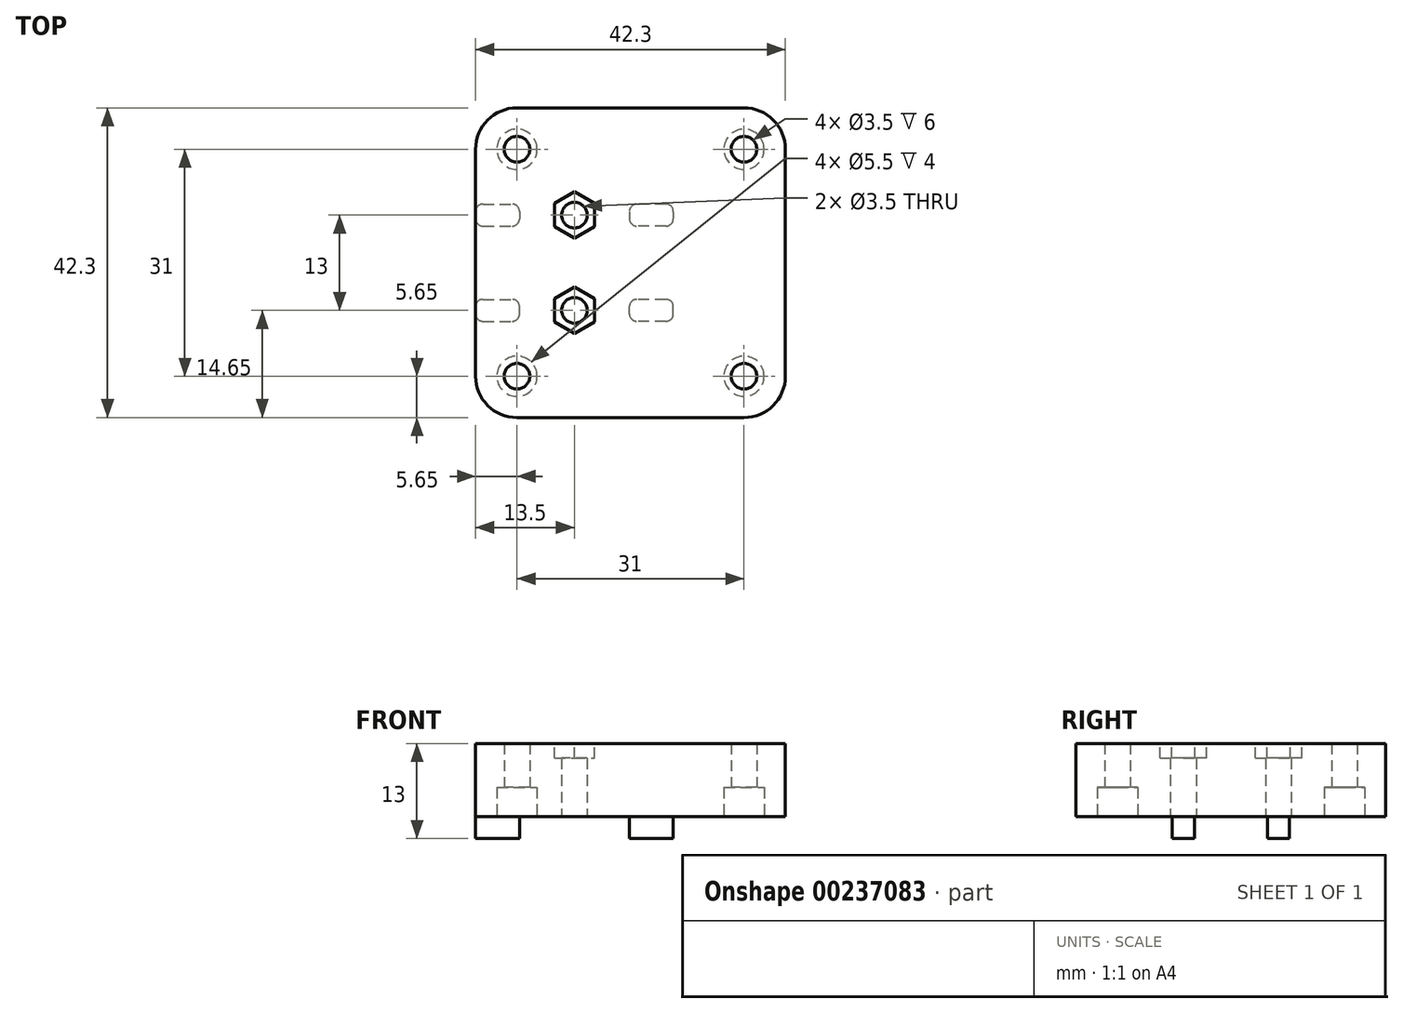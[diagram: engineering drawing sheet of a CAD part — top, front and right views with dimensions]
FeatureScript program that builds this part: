
annotation { "Feature Type Name" : "Feature", "Feature Type Description" : "" }
export const myFeature = defineFeature(function(context is Context, id is Id, definition is map)
    precondition{}
    {
        {
            var Q0;
            Q0=qCreatedBy(makeId("Top.planeOp"),FACE);
            var sketch = newSketch(context, id + "F0", { "sketchPlane" : qUnion([Q0])});
            skLineSegment(sketch, "E0.bottom", {"start": v(15.5, -15.5) * mm, "end": v(-15.5, -15.5) * mm, "construction": true});
            skLineSegment(sketch, "E0.top", {"start": v(15.5, 15.5) * mm, "end": v(-15.5, 15.5) * mm, "construction": true});
            skLineSegment(sketch, "E0.left", {"start": v(15.5, -15.5) * mm, "end": v(15.5, 15.5) * mm, "construction": true});
            skLineSegment(sketch, "E0.right", {"start": v(-15.5, -15.5) * mm, "end": v(-15.5, 15.5) * mm, "construction": true});
            skPoint(sketch, "E0.middle", {"position": v(0, 0) * mm});
            skCircle(sketch, "E1", {"center": v(-15.5, 15.5) * mm, "radius": 1.75 * mm});
            skCircle(sketch, "E2", {"center": v(15.5, 15.5) * mm, "radius": 1.75 * mm});
            skCircle(sketch, "E3", {"center": v(15.5, -15.5) * mm, "radius": 1.75 * mm});
            skCircle(sketch, "E4", {"center": v(-15.5, -15.5) * mm, "radius": 1.75 * mm});
            skLineSegment(sketch, "E5.bottom", {"start": v(15.5, -21.15) * mm, "end": v(-15.5, -21.15) * mm});
            skLineSegment(sketch, "E5.top", {"start": v(15.5, 21.15) * mm, "end": v(-15.5, 21.15) * mm});
            skLineSegment(sketch, "E5.left", {"start": v(21.15, -15.5) * mm, "end": v(21.15, 15.5) * mm});
            skLineSegment(sketch, "E5.right", {"start": v(-21.15, -15.5) * mm, "end": v(-21.15, 15.5) * mm});
            skPoint(sketch, "E6.visualSharp", {"position": v(-21.15, 21.15) * mm});
            skArc(sketch, "E6.filletArc", {"start": v(-15.5, 21.15) * mm, "mid": v(-19.5, 19.5) * mm, "end": v(-21.15, 15.5) * mm});
            skPoint(sketch, "E7.visualSharp", {"position": v(-21.15, -21.15) * mm});
            skArc(sketch, "E7.filletArc", {"start": v(-21.15, -15.5) * mm, "mid": v(-19.5, -19.5) * mm, "end": v(-15.5, -21.15) * mm});
            skPoint(sketch, "E8.visualSharp", {"position": v(21.15, -21.15) * mm});
            skArc(sketch, "E8.filletArc", {"start": v(15.5, -21.15) * mm, "mid": v(19.5, -19.5) * mm, "end": v(21.15, -15.5) * mm});
            skPoint(sketch, "E9.visualSharp", {"position": v(21.15, 21.15) * mm});
            skArc(sketch, "E9.filletArc", {"start": v(21.15, 15.5) * mm, "mid": v(19.5, 19.5) * mm, "end": v(15.5, 21.15) * mm});
            skSolve(sketch);
        }
        {
            var Q0;
            Q0=makeQuery(id+"F0.imprint","IMPRINT",FACE,{"disambiguationData":[TD([[makeQuery(id+"F0.imprint","IMPRINT",EDGE,{"derivedFrom":sQuery(id+"F0.wireOp",EDGE,"E1")}),-1.0]])]});
            extrude(context, id + "F1", {"entities" : qUnion([Q0]), "depth" : 10 * mm});
        }
        {
            var Q0;
            Q0=makeQuery(id+"F1.opExtrude","CAP_FACE",FACE,{"disambiguationData":[OSD([sQuery(id+"F0.wireOp",EDGE,"E1"),sQuery(id+"F0.wireOp",EDGE,"E2"),sQuery(id+"F0.wireOp",EDGE,"E3"),sQuery(id+"F0.wireOp",EDGE,"E4"),sQuery(id+"F0.wireOp",EDGE,"E5.bottom"),sQuery(id+"F0.wireOp",EDGE,"E5.top"),sQuery(id+"F0.wireOp",EDGE,"E5.left"),sQuery(id+"F0.wireOp",EDGE,"E5.right"),sQuery(id+"F0.wireOp",EDGE,"E6.filletArc"),sQuery(id+"F0.wireOp",EDGE,"E7.filletArc"),sQuery(id+"F0.wireOp",EDGE,"E8.filletArc"),sQuery(id+"F0.wireOp",EDGE,"E9.filletArc")])],"isStart":true});
            var sketch = newSketch(context, id + "F2", { "sketchPlane" : qUnion([Q0])});
            skCircle(sketch, "E10", {"center": v(15.5, 15.5) * mm, "radius": 2.75 * mm});
            skCircle(sketch, "E11", {"center": v(15.5, -15.5) * mm, "radius": 2.75 * mm});
            skCircle(sketch, "E12", {"center": v(-15.5, 15.5) * mm, "radius": 2.75 * mm});
            skCircle(sketch, "E13", {"center": v(-15.5, -15.5) * mm, "radius": 2.75 * mm});
            skSolve(sketch);
        }
        {
            var Q0;
            Q0=makeQuery(id+"F2.imprint","IMPRINT",FACE,{"disambiguationData":[TD([[makeQuery(id+"F2.imprint","IMPRINT",EDGE,{"derivedFrom":sQuery(id+"F2.wireOp",EDGE,"E10")}),1.0]])]});
            var Q1;
            Q1=makeQuery(id+"F2.imprint","IMPRINT",FACE,{"disambiguationData":[TD([[makeQuery(id+"F2.imprint","IMPRINT",EDGE,{"derivedFrom":sQuery(id+"F2.wireOp",EDGE,"E11")}),1.0]])]});
            var Q2;
            Q2=makeQuery(id+"F2.imprint","IMPRINT",FACE,{"disambiguationData":[TD([[makeQuery(id+"F2.imprint","IMPRINT",EDGE,{"derivedFrom":sQuery(id+"F2.wireOp",EDGE,"E13")}),1.0]])]});
            var Q3;
            Q3=makeQuery(id+"F2.imprint","IMPRINT",FACE,{"disambiguationData":[TD([[makeQuery(id+"F2.imprint","IMPRINT",EDGE,{"derivedFrom":sQuery(id+"F2.wireOp",EDGE,"E12")}),1.0]])]});
            extrude(context, id + "F3", {"entities" : qUnion([Q0, Q1, Q2, Q3]), "operationType" : NewBodyOperationType.REMOVE, "oppositeDirection" : true, "depth" : 4 * mm});
        }
        {
            var Q0;
            Q0=makeQuery(id+"F2.imprint","IMPRINT",FACE,{"disambiguationData":[TD([[makeQuery(id+"F2.imprint","IMPRINT",EDGE,{"derivedFrom":sQuery(id+"F2.wireOp",EDGE,"E10")}),-1.0]])]});
            var sketch = newSketch(context, id + "F4", { "sketchPlane" : qUnion([Q0])});
            skLineSegment(sketch, "E14.bottom", {"start": v(-21.15, -6.5) * mm, "end": v(5.85, -6.5) * mm, "construction": true});
            skLineSegment(sketch, "E14.top", {"start": v(-21.15, 6.5) * mm, "end": v(5.85, 6.5) * mm, "construction": true});
            skLineSegment(sketch, "E14.left", {"start": v(-21.15, 6.5) * mm, "end": v(-21.15, -6.5) * mm, "construction": true});
            skLineSegment(sketch, "E14.right", {"start": v(5.85, 6.5) * mm, "end": v(5.85, -6.5) * mm, "construction": true});
            skPoint(sketch, "E14.middle", {"position": v(-7.65, 0) * mm});
            skLineSegment(sketch, "E15.bottom", {"start": v(5.85, -8) * mm, "end": v(-0.15, -8) * mm});
            skLineSegment(sketch, "E15.top", {"start": v(5.85, -5) * mm, "end": v(-0.15, -5) * mm});
            skLineSegment(sketch, "E15.left", {"start": v(5.85, -8) * mm, "end": v(5.85, -5) * mm});
            skLineSegment(sketch, "E15.right", {"start": v(-0.15, -8) * mm, "end": v(-0.15, -5) * mm});
            skPoint(sketch, "E15.middle", {"position": v(2.85, -6.5) * mm});
            skLineSegment(sketch, "E16.bottom", {"start": v(5.85, 8) * mm, "end": v(-0.15, 8) * mm});
            skLineSegment(sketch, "E16.top", {"start": v(5.85, 5) * mm, "end": v(-0.15, 5) * mm});
            skLineSegment(sketch, "E16.left", {"start": v(5.85, 8) * mm, "end": v(5.85, 5) * mm});
            skLineSegment(sketch, "E16.right", {"start": v(-0.15, 8) * mm, "end": v(-0.15, 5) * mm});
            skPoint(sketch, "E16.middle", {"position": v(2.85, 6.5) * mm});
            skLineSegment(sketch, "E17.bottom", {"start": v(-21.15, -8) * mm, "end": v(-15.15, -8) * mm});
            skLineSegment(sketch, "E17.top", {"start": v(-21.15, -5) * mm, "end": v(-15.15, -5) * mm});
            skLineSegment(sketch, "E17.left", {"start": v(-21.15, -8) * mm, "end": v(-21.15, -5) * mm});
            skLineSegment(sketch, "E17.right", {"start": v(-15.15, -8) * mm, "end": v(-15.15, -5) * mm});
            skPoint(sketch, "E17.middle", {"position": v(-18.15, -6.5) * mm});
            skLineSegment(sketch, "E18.bottom", {"start": v(-21.15, 8) * mm, "end": v(-15.15, 8) * mm});
            skLineSegment(sketch, "E18.top", {"start": v(-21.15, 5) * mm, "end": v(-15.15, 5) * mm});
            skLineSegment(sketch, "E18.left", {"start": v(-21.15, 8) * mm, "end": v(-21.15, 5) * mm});
            skLineSegment(sketch, "E18.right", {"start": v(-15.15, 8) * mm, "end": v(-15.15, 5) * mm});
            skPoint(sketch, "E18.middle", {"position": v(-18.15, 6.5) * mm});
            skCircle(sketch, "E19", {"center": v(-7.65, 6.5) * mm, "radius": 1.75 * mm});
            skCircle(sketch, "E20", {"center": v(-7.65, -6.5) * mm, "radius": 1.75 * mm});
            skSolve(sketch);
        }
        {
            var Q0;
            Q0=makeQuery(id+"F4.imprint","IMPRINT",FACE,{"disambiguationData":[TD([[makeQuery(id+"F4.imprint","IMPRINT",EDGE,{"derivedFrom":sQuery(id+"F4.wireOp",EDGE,"E16.bottom")}),1.0]])]});
            var Q1;
            Q1=makeQuery(id+"F4.imprint","IMPRINT",FACE,{"disambiguationData":[TD([[makeQuery(id+"F4.imprint","IMPRINT",EDGE,{"derivedFrom":sQuery(id+"F4.wireOp",EDGE,"E17.bottom")}),1.0]])]});
            var Q2;
            Q2=makeQuery(id+"F4.imprint","IMPRINT",FACE,{"disambiguationData":[TD([[makeQuery(id+"F4.imprint","IMPRINT",EDGE,{"derivedFrom":sQuery(id+"F4.wireOp",EDGE,"E18.bottom")}),-1.0]])]});
            var Q3;
            Q3=makeQuery(id+"F4.imprint","IMPRINT",FACE,{"disambiguationData":[TD([[makeQuery(id+"F4.imprint","IMPRINT",EDGE,{"derivedFrom":sQuery(id+"F4.wireOp",EDGE,"E15.bottom")}),-1.0]])]});
            extrude(context, id + "F5", {"entities" : qUnion([Q0, Q1, Q2, Q3]), "operationType" : NewBodyOperationType.ADD, "depth" : 3 * mm});
        }
        {
            var Q0;
            Q0=makeQuery(id+"F5.opExtrude","SWEPT_EDGE",EDGE,{"disambiguationData":[OSD([sQuery(id+"F4.wireOp",EDGE,"E18.bottom"),sQuery(id+"F4.wireOp",EDGE,"E18.left")])]});
            var Q1;
            Q1=makeQuery(id+"F5.opExtrude","SWEPT_EDGE",EDGE,{"disambiguationData":[OSD([sQuery(id+"F4.wireOp",EDGE,"E18.top"),sQuery(id+"F4.wireOp",EDGE,"E18.left")])]});
            var Q2;
            Q2=makeQuery(id+"F5.opExtrude","SWEPT_EDGE",EDGE,{"disambiguationData":[OSD([sQuery(id+"F4.wireOp",EDGE,"E17.top"),sQuery(id+"F4.wireOp",EDGE,"E17.left")])]});
            var Q3;
            Q3=makeQuery(id+"F5.opExtrude","SWEPT_EDGE",EDGE,{"disambiguationData":[OSD([sQuery(id+"F4.wireOp",EDGE,"E17.top"),sQuery(id+"F4.wireOp",EDGE,"E17.right")])]});
            var Q4;
            Q4=makeQuery(id+"F5.opExtrude","SWEPT_EDGE",EDGE,{"disambiguationData":[OSD([sQuery(id+"F4.wireOp",EDGE,"E18.bottom"),sQuery(id+"F4.wireOp",EDGE,"E18.right")])]});
            var Q5;
            Q5=makeQuery(id+"F5.opExtrude","SWEPT_EDGE",EDGE,{"disambiguationData":[OSD([sQuery(id+"F4.wireOp",EDGE,"E16.bottom"),sQuery(id+"F4.wireOp",EDGE,"E16.right")])]});
            var Q6;
            Q6=makeQuery(id+"F5.opExtrude","SWEPT_EDGE",EDGE,{"disambiguationData":[OSD([sQuery(id+"F4.wireOp",EDGE,"E16.top"),sQuery(id+"F4.wireOp",EDGE,"E16.right")])]});
            var Q7;
            Q7=makeQuery(id+"F5.opExtrude","SWEPT_EDGE",EDGE,{"disambiguationData":[OSD([sQuery(id+"F4.wireOp",EDGE,"E15.top"),sQuery(id+"F4.wireOp",EDGE,"E15.right")])]});
            var Q8;
            Q8=makeQuery(id+"F5.opExtrude","SWEPT_EDGE",EDGE,{"disambiguationData":[OSD([sQuery(id+"F4.wireOp",EDGE,"E15.bottom"),sQuery(id+"F4.wireOp",EDGE,"E15.right")])]});
            var Q9;
            Q9=makeQuery(id+"F5.opExtrude","SWEPT_EDGE",EDGE,{"disambiguationData":[OSD([sQuery(id+"F4.wireOp",EDGE,"E16.bottom"),sQuery(id+"F4.wireOp",EDGE,"E16.left")])]});
            var Q10;
            Q10=makeQuery(id+"F5.opExtrude","SWEPT_EDGE",EDGE,{"disambiguationData":[OSD([sQuery(id+"F4.wireOp",EDGE,"E15.top"),sQuery(id+"F4.wireOp",EDGE,"E15.left")])]});
            var Q11;
            Q11=makeQuery(id+"F5.opExtrude","SWEPT_EDGE",EDGE,{"disambiguationData":[OSD([sQuery(id+"F4.wireOp",EDGE,"E16.top"),sQuery(id+"F4.wireOp",EDGE,"E16.left")])]});
            var Q12;
            Q12=makeQuery(id+"F5.opExtrude","SWEPT_EDGE",EDGE,{"disambiguationData":[OSD([sQuery(id+"F4.wireOp",EDGE,"E15.bottom"),sQuery(id+"F4.wireOp",EDGE,"E15.left")])]});
            var Q13;
            Q13=makeQuery(id+"F5.opExtrude","SWEPT_EDGE",EDGE,{"disambiguationData":[OSD([sQuery(id+"F4.wireOp",EDGE,"E17.bottom"),sQuery(id+"F4.wireOp",EDGE,"E17.right")])]});
            var Q14;
            Q14=makeQuery(id+"F5.opExtrude","SWEPT_EDGE",EDGE,{"disambiguationData":[OSD([sQuery(id+"F4.wireOp",EDGE,"E17.bottom"),sQuery(id+"F4.wireOp",EDGE,"E17.left")])]});
            var Q15;
            Q15=makeQuery(id+"F5.opExtrude","SWEPT_EDGE",EDGE,{"disambiguationData":[OSD([sQuery(id+"F4.wireOp",EDGE,"E18.top"),sQuery(id+"F4.wireOp",EDGE,"E18.right")])]});
            fillet(context, id + "F6", {"entities" : qUnion([Q0, Q1, Q2, Q3, Q4, Q5, Q6, Q7, Q8, Q9, Q10, Q11, Q12, Q13, Q14, Q15]), "radius" : 1 * mm, "tangentPropagation" : true, "allowEdgeOverflow" : false});
        }
        {
            var Q0;
            Q0=makeQuery(id+"F4.imprint","IMPRINT",FACE,{"disambiguationData":[TD([[makeQuery(id+"F4.imprint","IMPRINT",EDGE,{"derivedFrom":sQuery(id+"F4.wireOp",EDGE,"E19")}),1.0]])]});
            var Q1;
            Q1=makeQuery(id+"F4.imprint","IMPRINT",FACE,{"disambiguationData":[TD([[makeQuery(id+"F4.imprint","IMPRINT",EDGE,{"derivedFrom":sQuery(id+"F4.wireOp",EDGE,"E20")}),1.0]])]});
            extrude(context, id + "F7", {"entities" : qUnion([Q0, Q1]), "operationType" : NewBodyOperationType.REMOVE, "oppositeDirection" : true, "depth" : 25 * mm});
        }
        {
            var Q0;
            Q0=makeQuery(id+"F1.opExtrude","CAP_FACE",FACE,{"disambiguationData":[OSD([sQuery(id+"F0.wireOp",EDGE,"E1"),sQuery(id+"F0.wireOp",EDGE,"E2"),sQuery(id+"F0.wireOp",EDGE,"E3"),sQuery(id+"F0.wireOp",EDGE,"E4"),sQuery(id+"F0.wireOp",EDGE,"E5.bottom"),sQuery(id+"F0.wireOp",EDGE,"E5.top"),sQuery(id+"F0.wireOp",EDGE,"E5.left"),sQuery(id+"F0.wireOp",EDGE,"E5.right"),sQuery(id+"F0.wireOp",EDGE,"E6.filletArc"),sQuery(id+"F0.wireOp",EDGE,"E7.filletArc"),sQuery(id+"F0.wireOp",EDGE,"E8.filletArc"),sQuery(id+"F0.wireOp",EDGE,"E9.filletArc")])],"isStart":false});
            var sketch = newSketch(context, id + "F8", { "sketchPlane" : qUnion([Q0])});
            skCircle(sketch, "E21.cCircle", {"center": v(-7.65, 6.5) * mm, "radius": 2.75 * mm, "construction": true});
            skLineSegment(sketch, "E21.0", {"start": v(-4.9, 8.09) * mm, "end": v(-4.9, 4.91) * mm});
            skLineSegment(sketch, "E21.1", {"start": v(-4.9, 4.91) * mm, "end": v(-7.65, 3.32) * mm});
            skLineSegment(sketch, "E21.2", {"start": v(-7.65, 3.32) * mm, "end": v(-10.4, 4.91) * mm});
            skLineSegment(sketch, "E21.3", {"start": v(-10.4, 4.91) * mm, "end": v(-10.4, 8.09) * mm});
            skLineSegment(sketch, "E21.4", {"start": v(-10.4, 8.09) * mm, "end": v(-7.65, 9.68) * mm});
            skLineSegment(sketch, "E21.5", {"start": v(-7.65, 9.68) * mm, "end": v(-4.9, 8.09) * mm});
            skPoint(sketch, "E21.0.midPoint", {"position": v(-4.9, 6.5) * mm});
            skCircle(sketch, "E22.cCircle", {"center": v(-7.65, -6.5) * mm, "radius": 2.75 * mm, "construction": true});
            skLineSegment(sketch, "E22.0", {"start": v(-4.9, -4.91) * mm, "end": v(-4.9, -8.09) * mm});
            skLineSegment(sketch, "E22.1", {"start": v(-4.9, -8.09) * mm, "end": v(-7.65, -9.68) * mm});
            skLineSegment(sketch, "E22.2", {"start": v(-7.65, -9.68) * mm, "end": v(-10.4, -8.09) * mm});
            skLineSegment(sketch, "E22.3", {"start": v(-10.4, -8.09) * mm, "end": v(-10.4, -4.91) * mm});
            skLineSegment(sketch, "E22.4", {"start": v(-10.4, -4.91) * mm, "end": v(-7.65, -3.32) * mm});
            skLineSegment(sketch, "E22.5", {"start": v(-7.65, -3.32) * mm, "end": v(-4.9, -4.91) * mm});
            skPoint(sketch, "E22.0.midPoint", {"position": v(-4.9, -6.5) * mm});
            skSolve(sketch);
        }
        {
            var Q0;
            Q0 = qSketchRegion(id + "F8", true);
            extrude(context, id + "F9", {"entities" : qUnion([Q0]), "operationType" : NewBodyOperationType.REMOVE, "oppositeDirection" : true, "depth" : 2 * mm});
        }
    });
